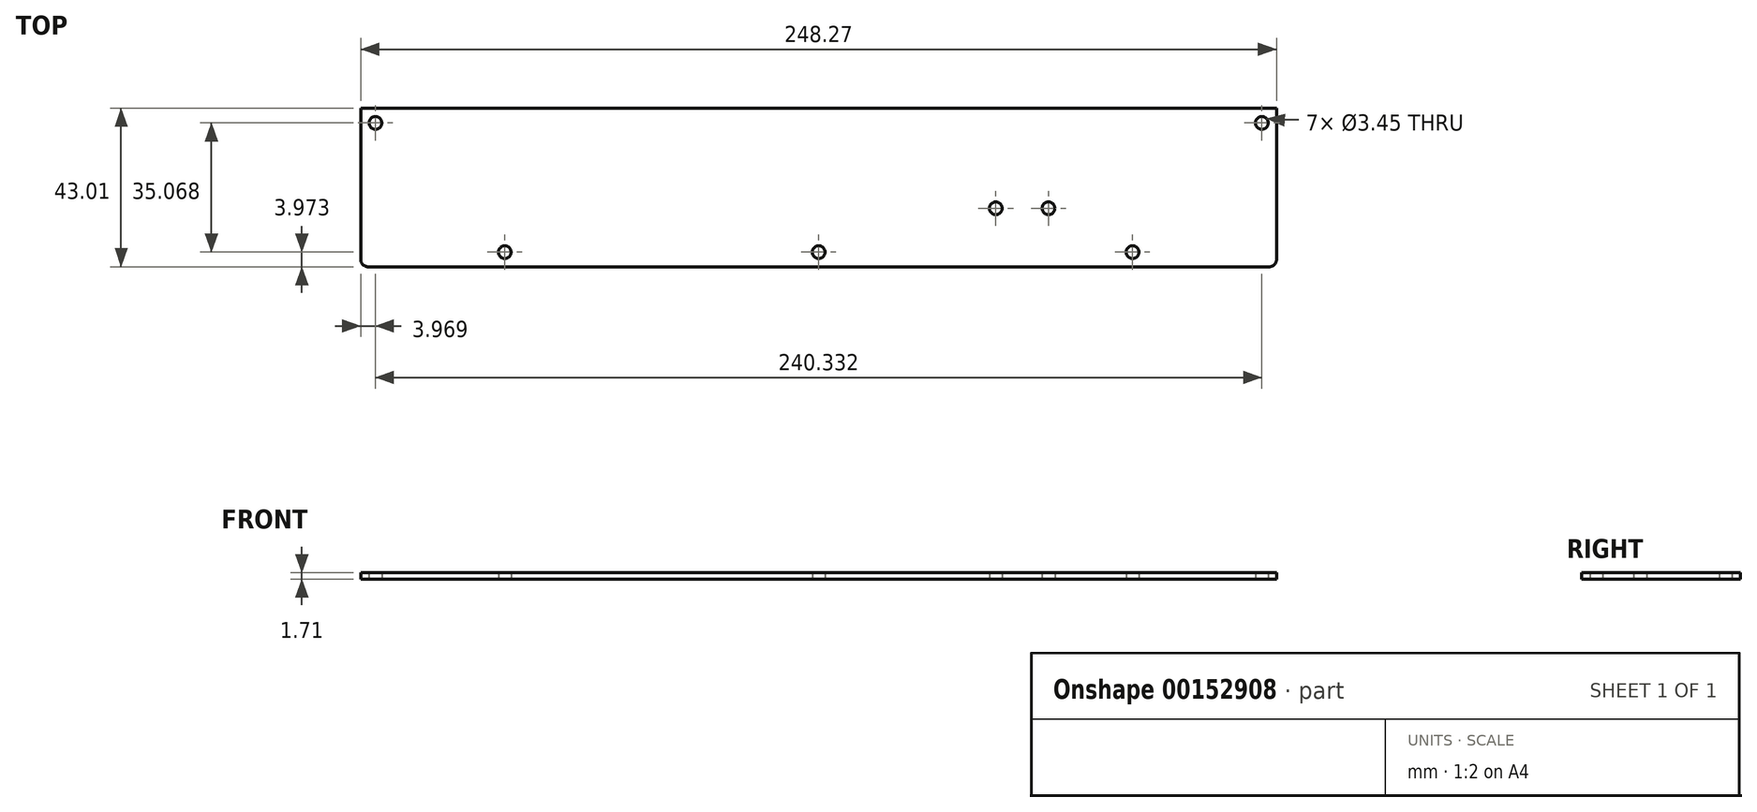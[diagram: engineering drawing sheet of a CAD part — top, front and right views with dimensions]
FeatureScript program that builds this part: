
annotation { "Feature Type Name" : "Feature", "Feature Type Description" : "" }
export const myFeature = defineFeature(function(context is Context, id is Id, definition is map)
    precondition{}
    {
        {
            var Q0;
            Q0=qCreatedBy(makeId("Top.planeOp"),FACE);
            var sketch = newSketch(context, id + "F0", { "sketchPlane" : qUnion([Q0])});
            skLineSegment(sketch, "E0.bottom", {"start": v(0, 0) * mm, "end": v(248.27, 0) * mm});
            skLineSegment(sketch, "E0.top", {"start": v(0, -43) * mm, "end": v(248.27, -43) * mm});
            skLineSegment(sketch, "E0.left", {"start": v(0, 0) * mm, "end": v(0, -43) * mm});
            skLineSegment(sketch, "E0.right", {"start": v(248.27, 0) * mm, "end": v(248.27, -43) * mm});
            skLineSegment(sketch, "E1", {"start": v(0, -3.97) * mm, "end": v(3.97, -3.97) * mm, "construction": true});
            skLineSegment(sketch, "E2", {"start": v(3.97, -3.97) * mm, "end": v(3.97, 0) * mm, "construction": true});
            skLineSegment(sketch, "E3", {"start": v(244.3, 0) * mm, "end": v(244.3, -3.97) * mm, "construction": true});
            skLineSegment(sketch, "E4", {"start": v(244.3, -3.97) * mm, "end": v(248.27, -3.97) * mm, "construction": true});
            skLineSegment(sketch, "E5", {"start": v(124.13, -43) * mm, "end": v(124.13, -39.04) * mm, "construction": true});
            skLineSegment(sketch, "E6", {"start": v(124.13, -39.04) * mm, "end": v(209.23, -39.04) * mm, "construction": true});
            skLineSegment(sketch, "E7", {"start": v(124.13, -39.04) * mm, "end": v(39.04, -39.04) * mm, "construction": true});
            skCircle(sketch, "E8", {"center": v(3.97, -3.97) * mm, "radius": 1.73 * mm});
            skCircle(sketch, "E9", {"center": v(39.04, -39.04) * mm, "radius": 1.73 * mm});
            skCircle(sketch, "E10", {"center": v(124.13, -39.04) * mm, "radius": 1.73 * mm});
            skCircle(sketch, "E11", {"center": v(209.23, -39.04) * mm, "radius": 1.73 * mm});
            skCircle(sketch, "E12", {"center": v(244.3, -3.97) * mm, "radius": 1.73 * mm});
            skLineSegment(sketch, "E13", {"start": v(209.23, -39.04) * mm, "end": v(209.23, -3.97) * mm, "construction": true});
            skLineSegment(sketch, "E14", {"start": v(209.23, -3.97) * mm, "end": v(244.3, -3.97) * mm, "construction": true});
            skLineSegment(sketch, "E15", {"start": v(124.13, -39.04) * mm, "end": v(124.13, -27.15) * mm, "construction": true});
            skLineSegment(sketch, "E16", {"start": v(124.13, -27.15) * mm, "end": v(186.46, -27.15) * mm, "construction": true});
            skLineSegment(sketch, "E17", {"start": v(172.17, -27.15) * mm, "end": v(186.46, -27.15) * mm, "construction": true});
            skPoint(sketch, "E18", {"position": v(179.31, -27.15) * mm});
            skCircle(sketch, "E19", {"center": v(186.46, -27.15) * mm, "radius": 1.73 * mm});
            skCircle(sketch, "E20", {"center": v(172.17, -27.15) * mm, "radius": 1.73 * mm});
            skSolve(sketch);
        }
        {
            var Q0;
            Q0=qSketchRegion(id+"F0",true);
            extrude(context, id + "F1", {"entities" : qUnion([Q0]), "depth" : 1.7 * mm});
        }
        {
            var Q0;
            Q0=makeQuery(id+"F1.opExtrude","SWEPT_EDGE",EDGE,{"disambiguationData":[OSD([sQuery(id+"F0.wireOp",EDGE,"E0.top"),sQuery(id+"F0.wireOp",EDGE,"E0.left")])]});
            var Q1;
            Q1=makeQuery(id+"F1.opExtrude","SWEPT_EDGE",EDGE,{"disambiguationData":[OSD([sQuery(id+"F0.wireOp",EDGE,"E0.top"),sQuery(id+"F0.wireOp",EDGE,"E0.right")])]});
            fillet(context, id + "F2", {"entities" : qUnion([Q0, Q1]), "radius" : 1.98 * mm, "tangentPropagation" : true, "allowEdgeOverflow" : false});
        }
    });
